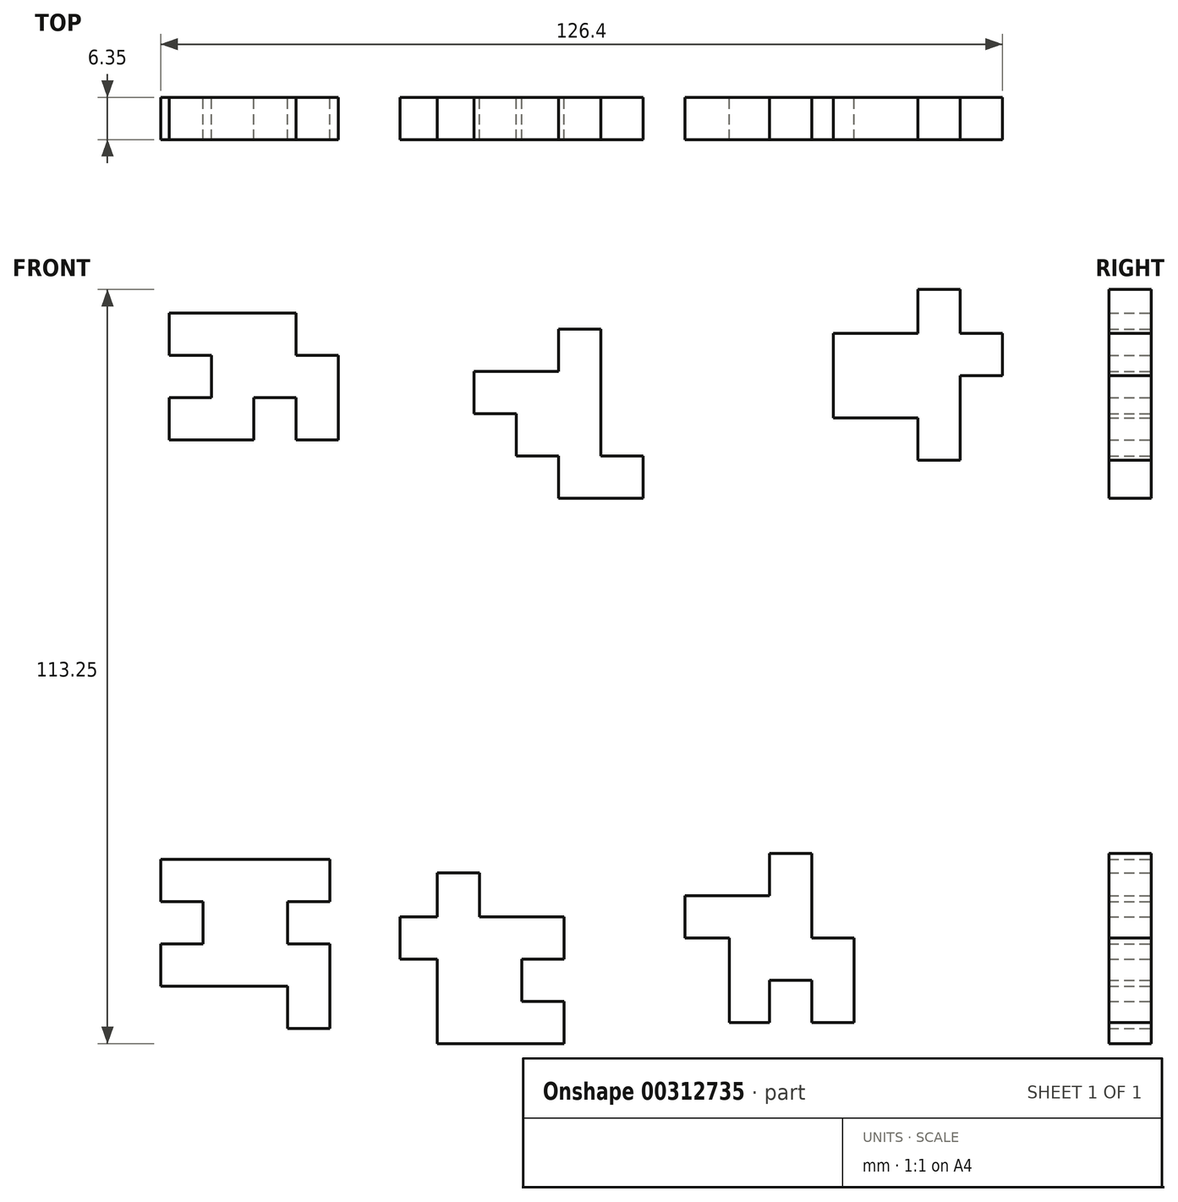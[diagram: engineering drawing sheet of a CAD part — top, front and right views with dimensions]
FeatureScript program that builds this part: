
annotation { "Feature Type Name" : "Feature", "Feature Type Description" : "" }
export const myFeature = defineFeature(function(context is Context, id is Id, definition is map)
    precondition{}
    {
        {
            var Q0;
            Q0=qCreatedBy(makeId("Front.planeOp"),FACE);
            var sketch = newSketch(context, id + "F0", { "sketchPlane" : qUnion([Q0])});
            skLineSegment(sketch, "E0", {"start": v(0, 46.22) * mm, "end": v(-6.35, 46.22) * mm});
            skLineSegment(sketch, "E1", {"start": v(-6.35, 46.22) * mm, "end": v(-6.35, 39.87) * mm});
            skLineSegment(sketch, "E2", {"start": v(-6.35, 39.87) * mm, "end": v(-19.05, 39.87) * mm});
            skLineSegment(sketch, "E3", {"start": v(-19.05, 39.87) * mm, "end": v(-19.05, 33.52) * mm});
            skLineSegment(sketch, "E4", {"start": v(-19.05, 33.52) * mm, "end": v(-12.7, 33.52) * mm});
            skLineSegment(sketch, "E5", {"start": v(-12.7, 33.52) * mm, "end": v(-12.7, 27.17) * mm});
            skLineSegment(sketch, "E6", {"start": v(-12.7, 27.17) * mm, "end": v(-6.35, 27.17) * mm});
            skLineSegment(sketch, "E7", {"start": v(-6.35, 27.17) * mm, "end": v(-6.35, 20.82) * mm});
            skLineSegment(sketch, "E8", {"start": v(6.35, 20.82) * mm, "end": v(-6.35, 20.82) * mm});
            skLineSegment(sketch, "E9", {"start": v(6.35, 20.82) * mm, "end": v(6.35, 27.17) * mm});
            skLineSegment(sketch, "E10", {"start": v(6.35, 27.17) * mm, "end": v(0, 27.17) * mm});
            skLineSegment(sketch, "E11", {"start": v(0, 27.17) * mm, "end": v(0, 46.22) * mm});
            skSolve(sketch);
        }
        {
            var Q0;
            Q0=makeQuery(id+"F0.imprint","IMPRINT",FACE,{"disambiguationData":[TD([[makeQuery(id+"F0.imprint","IMPRINT",EDGE,{"derivedFrom":sQuery(id+"F0.wireOp",EDGE,"E0")}),1.0]])]});
            extrude(context, id + "F1", {"entities" : qUnion([Q0]), "depth" : 6.35 * mm});
        }
        {
            var Q0;
            Q0=qCreatedBy(makeId("Front.planeOp"),FACE);
            var sketch = newSketch(context, id + "F2", { "sketchPlane" : qUnion([Q0])});
            skLineSegment(sketch, "E12", {"start": v(-64.79, 48.64) * mm, "end": v(-45.74, 48.64) * mm});
            skLineSegment(sketch, "E13", {"start": v(-45.74, 48.64) * mm, "end": v(-45.74, 42.3) * mm});
            skLineSegment(sketch, "E14", {"start": v(-39.39, 42.3) * mm, "end": v(-45.74, 42.3) * mm});
            skLineSegment(sketch, "E15", {"start": v(-39.39, 42.3) * mm, "end": v(-39.39, 29.6) * mm});
            skLineSegment(sketch, "E16", {"start": v(-39.39, 29.6) * mm, "end": v(-45.74, 29.6) * mm});
            skLineSegment(sketch, "E17", {"start": v(-45.74, 29.6) * mm, "end": v(-45.74, 35.94) * mm});
            skLineSegment(sketch, "E18", {"start": v(-45.74, 35.94) * mm, "end": v(-52.09, 35.94) * mm});
            skLineSegment(sketch, "E19", {"start": v(-52.09, 35.94) * mm, "end": v(-52.09, 29.6) * mm});
            skLineSegment(sketch, "E20", {"start": v(-52.09, 29.6) * mm, "end": v(-64.79, 29.6) * mm});
            skLineSegment(sketch, "E21", {"start": v(-64.79, 29.6) * mm, "end": v(-64.79, 35.94) * mm});
            skLineSegment(sketch, "E22", {"start": v(-64.79, 35.94) * mm, "end": v(-58.44, 35.94) * mm});
            skLineSegment(sketch, "E23", {"start": v(-58.44, 35.94) * mm, "end": v(-58.44, 42.3) * mm});
            skLineSegment(sketch, "E24", {"start": v(-58.44, 42.3) * mm, "end": v(-64.79, 42.3) * mm});
            skLineSegment(sketch, "E25", {"start": v(-64.79, 42.3) * mm, "end": v(-64.79, 48.64) * mm});
            skSolve(sketch);
        }
        {
            var Q0;
            Q0 = qSketchRegion(id + "F2", true);
            extrude(context, id + "F3", {"entities" : qUnion([Q0]), "depth" : 6.35 * mm});
        }
        {
            var Q0;
            Q0=qCreatedBy(makeId("Front.planeOp"),FACE);
            var sketch = newSketch(context, id + "F4", { "sketchPlane" : qUnion([Q0])});
            skLineSegment(sketch, "E26", {"start": v(34.94, 45.57) * mm, "end": v(34.94, 32.87) * mm});
            skLineSegment(sketch, "E27", {"start": v(34.94, 32.87) * mm, "end": v(47.64, 32.87) * mm});
            skLineSegment(sketch, "E28", {"start": v(47.64, 32.87) * mm, "end": v(47.64, 26.52) * mm});
            skLineSegment(sketch, "E29", {"start": v(47.64, 26.52) * mm, "end": v(54, 26.52) * mm});
            skLineSegment(sketch, "E30", {"start": v(54, 26.52) * mm, "end": v(54, 39.22) * mm});
            skLineSegment(sketch, "E31", {"start": v(54, 39.22) * mm, "end": v(60.34, 39.22) * mm});
            skLineSegment(sketch, "E32", {"start": v(60.34, 39.22) * mm, "end": v(60.34, 45.57) * mm});
            skLineSegment(sketch, "E33", {"start": v(60.34, 45.57) * mm, "end": v(54, 45.57) * mm});
            skLineSegment(sketch, "E34", {"start": v(54, 45.57) * mm, "end": v(54, 52.16) * mm});
            skLineSegment(sketch, "E35", {"start": v(54, 52.16) * mm, "end": v(47.64, 52.16) * mm});
            skLineSegment(sketch, "E36", {"start": v(47.64, 52.16) * mm, "end": v(47.64, 45.57) * mm});
            skLineSegment(sketch, "E37", {"start": v(47.64, 45.57) * mm, "end": v(34.94, 45.57) * mm});
            skSolve(sketch);
        }
        {
            var Q0;
            Q0=makeQuery(id+"F4.imprint","IMPRINT",FACE,{"disambiguationData":[TD([[makeQuery(id+"F4.imprint","IMPRINT",EDGE,{"derivedFrom":sQuery(id+"F4.wireOp",EDGE,"E26")}),1.0]])]});
            extrude(context, id + "F5", {"entities" : qUnion([Q0]), "depth" : 6.35 * mm});
        }
        {
            var Q0;
            Q0=qCreatedBy(makeId("Front.planeOp"),FACE);
            var sketch = newSketch(context, id + "F6", { "sketchPlane" : qUnion([Q0])});
            skLineSegment(sketch, "E38", {"start": v(-66.06, -52.5) * mm, "end": v(-66.06, -46.16) * mm});
            skLineSegment(sketch, "E39", {"start": v(-66.06, -46.16) * mm, "end": v(-59.7, -46.16) * mm});
            skLineSegment(sketch, "E40", {"start": v(-59.7, -46.16) * mm, "end": v(-59.7, -39.8) * mm});
            skLineSegment(sketch, "E41", {"start": v(-59.7, -39.8) * mm, "end": v(-66.06, -39.8) * mm});
            skLineSegment(sketch, "E42", {"start": v(-66.06, -39.8) * mm, "end": v(-66.06, -33.46) * mm});
            skLineSegment(sketch, "E43", {"start": v(-66.06, -33.46) * mm, "end": v(-40.66, -33.46) * mm});
            skLineSegment(sketch, "E44", {"start": v(-40.66, -33.46) * mm, "end": v(-40.66, -39.8) * mm});
            skLineSegment(sketch, "E45", {"start": v(-40.66, -39.8) * mm, "end": v(-47, -39.8) * mm});
            skLineSegment(sketch, "E46", {"start": v(-47, -39.8) * mm, "end": v(-47, -46.16) * mm});
            skLineSegment(sketch, "E47", {"start": v(-47, -46.16) * mm, "end": v(-40.66, -46.16) * mm});
            skLineSegment(sketch, "E48", {"start": v(-40.66, -46.16) * mm, "end": v(-40.66, -58.86) * mm});
            skLineSegment(sketch, "E49", {"start": v(-40.66, -58.86) * mm, "end": v(-47, -58.86) * mm});
            skLineSegment(sketch, "E50", {"start": v(-47, -58.86) * mm, "end": v(-47, -52.5) * mm});
            skLineSegment(sketch, "E51", {"start": v(-47, -52.5) * mm, "end": v(-66.06, -52.5) * mm});
            skSolve(sketch);
        }
        {
            var Q0;
            Q0=makeQuery(id+"F6.imprint","IMPRINT",FACE,{"disambiguationData":[TD([[makeQuery(id+"F6.imprint","IMPRINT",EDGE,{"derivedFrom":sQuery(id+"F6.wireOp",EDGE,"E38")}),-1.0]])]});
            extrude(context, id + "F7", {"entities" : qUnion([Q0]), "depth" : 6.35 * mm});
        }
        {
            var Q0;
            Q0=qCreatedBy(makeId("Front.planeOp"),FACE);
            var sketch = newSketch(context, id + "F8", { "sketchPlane" : qUnion([Q0])});
            skLineSegment(sketch, "E52", {"start": v(-24.55, -61.1) * mm, "end": v(-5.5, -61.1) * mm});
            skLineSegment(sketch, "E53", {"start": v(-5.5, -61.1) * mm, "end": v(-5.5, -54.74) * mm});
            skLineSegment(sketch, "E54", {"start": v(-5.5, -54.74) * mm, "end": v(-11.85, -54.74) * mm});
            skLineSegment(sketch, "E55", {"start": v(-11.85, -54.74) * mm, "end": v(-11.85, -48.4) * mm});
            skLineSegment(sketch, "E56", {"start": v(-11.85, -48.4) * mm, "end": v(-5.5, -48.4) * mm});
            skLineSegment(sketch, "E57", {"start": v(-5.5, -48.4) * mm, "end": v(-5.5, -42.04) * mm});
            skLineSegment(sketch, "E58", {"start": v(-5.5, -42.04) * mm, "end": v(-18.2, -42.04) * mm});
            skLineSegment(sketch, "E59", {"start": v(-18.2, -42.04) * mm, "end": v(-18.2, -35.45) * mm});
            skLineSegment(sketch, "E60", {"start": v(-18.2, -35.45) * mm, "end": v(-24.55, -35.45) * mm});
            skLineSegment(sketch, "E61", {"start": v(-24.55, -35.45) * mm, "end": v(-24.55, -42.04) * mm});
            skLineSegment(sketch, "E62", {"start": v(-24.55, -42.04) * mm, "end": v(-30.16, -42.04) * mm});
            skLineSegment(sketch, "E63", {"start": v(-30.16, -42.04) * mm, "end": v(-30.16, -48.4) * mm});
            skLineSegment(sketch, "E64", {"start": v(-30.16, -48.4) * mm, "end": v(-24.55, -48.4) * mm});
            skLineSegment(sketch, "E65", {"start": v(-24.55, -48.4) * mm, "end": v(-24.55, -61.1) * mm});
            skSolve(sketch);
        }
        {
            var Q0;
            Q0=makeQuery(id+"F8.imprint","IMPRINT",FACE,{"disambiguationData":[TD([[makeQuery(id+"F8.imprint","IMPRINT",EDGE,{"derivedFrom":sQuery(id+"F8.wireOp",EDGE,"E52")}),1.0]])]});
            extrude(context, id + "F9", {"entities" : qUnion([Q0]), "depth" : 6.35 * mm});
        }
        {
            var Q0;
            Q0=qCreatedBy(makeId("Front.planeOp"),FACE);
            var sketch = newSketch(context, id + "F10", { "sketchPlane" : qUnion([Q0])});
            skLineSegment(sketch, "E66", {"start": v(19.37, -57.91) * mm, "end": v(19.37, -45.21) * mm});
            skLineSegment(sketch, "E67", {"start": v(19.37, -45.21) * mm, "end": v(12.66, -45.21) * mm});
            skLineSegment(sketch, "E68", {"start": v(12.66, -45.21) * mm, "end": v(12.66, -38.86) * mm});
            skLineSegment(sketch, "E69", {"start": v(12.66, -38.86) * mm, "end": v(25.36, -38.86) * mm});
            skLineSegment(sketch, "E70", {"start": v(25.36, -38.86) * mm, "end": v(25.36, -32.51) * mm});
            skLineSegment(sketch, "E71", {"start": v(25.36, -32.51) * mm, "end": v(31.7, -32.51) * mm});
            skLineSegment(sketch, "E72", {"start": v(31.7, -32.51) * mm, "end": v(31.7, -45.21) * mm});
            skLineSegment(sketch, "E73", {"start": v(31.7, -45.21) * mm, "end": v(38.06, -45.21) * mm});
            skLineSegment(sketch, "E74", {"start": v(38.06, -45.21) * mm, "end": v(38.06, -57.91) * mm});
            skLineSegment(sketch, "E75", {"start": v(38.06, -57.91) * mm, "end": v(31.7, -57.91) * mm});
            skLineSegment(sketch, "E76", {"start": v(31.7, -57.91) * mm, "end": v(31.7, -51.56) * mm});
            skLineSegment(sketch, "E77", {"start": v(31.7, -51.56) * mm, "end": v(25.36, -51.56) * mm});
            skLineSegment(sketch, "E78", {"start": v(25.36, -51.56) * mm, "end": v(25.36, -57.91) * mm});
            skLineSegment(sketch, "E79", {"start": v(25.36, -57.91) * mm, "end": v(19.37, -57.91) * mm});
            skSolve(sketch);
        }
        {
            var Q0;
            Q0=makeQuery(id+"F10.imprint","IMPRINT",FACE,{"disambiguationData":[TD([[makeQuery(id+"F10.imprint","IMPRINT",EDGE,{"derivedFrom":sQuery(id+"F10.wireOp",EDGE,"E66")}),-1.0]])]});
            extrude(context, id + "F11", {"entities" : qUnion([Q0]), "depth" : 6.35 * mm});
        }
    });
